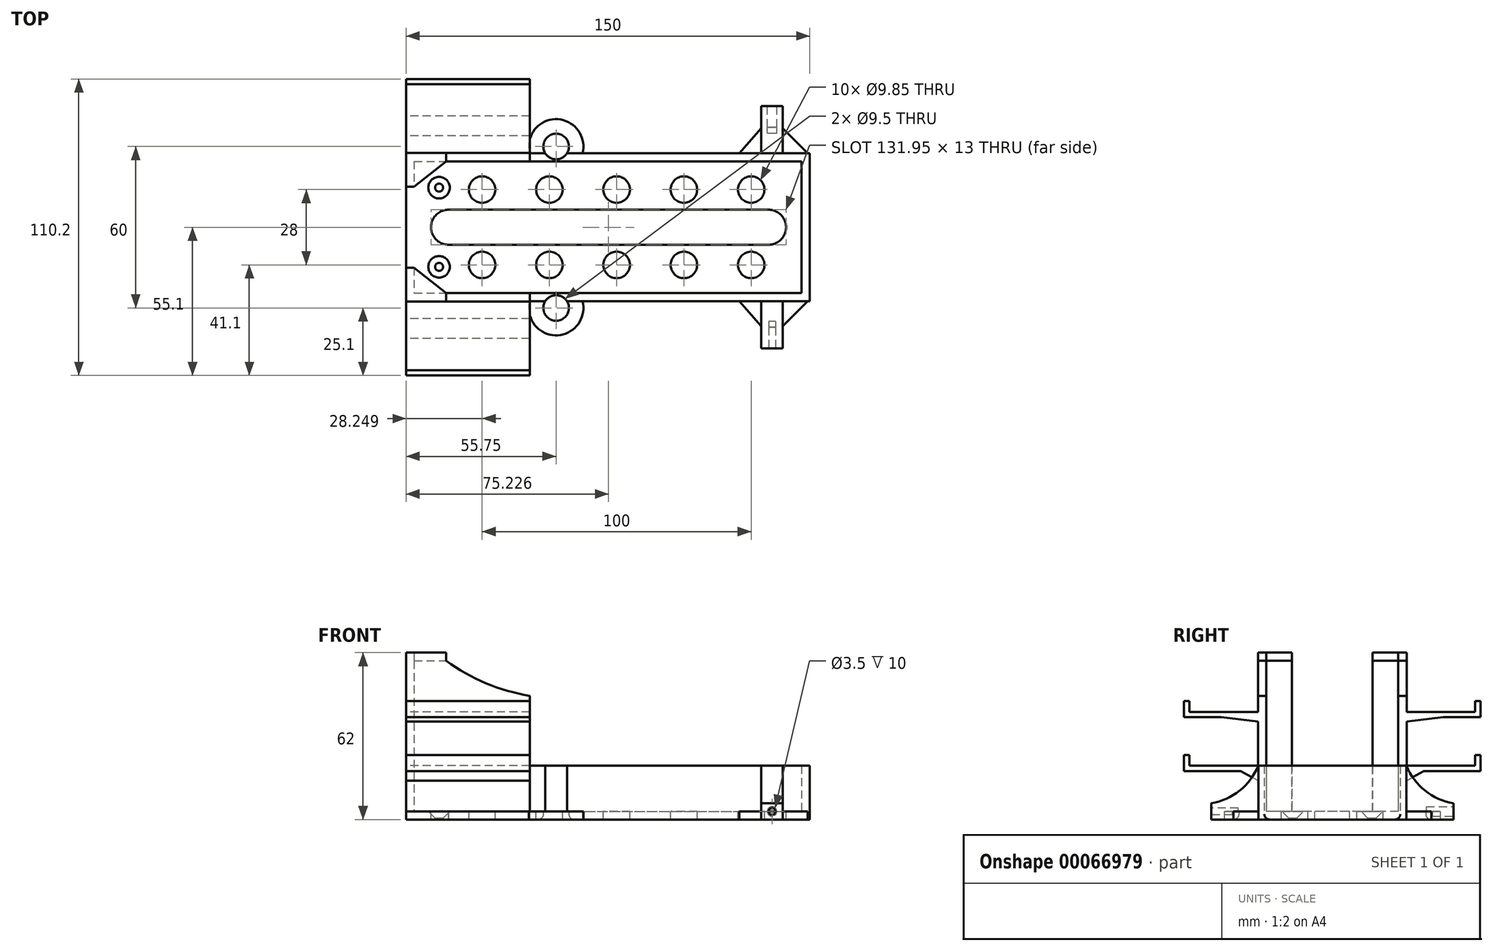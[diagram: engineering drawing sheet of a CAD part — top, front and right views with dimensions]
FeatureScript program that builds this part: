
annotation { "Feature Type Name" : "Feature", "Feature Type Description" : "" }
export const myFeature = defineFeature(function(context is Context, id is Id, definition is map)
    precondition{}
    {
        {
            var Q0;
            Q0=qCreatedBy(makeId("Top.planeOp"),FACE);
            var sketch = newSketch(context, id + "F0", { "sketchPlane" : qUnion([Q0])});
            skLineSegment(sketch, "E0.bottom", {"start": v(0, 27.5) * mm, "end": v(150, 27.5) * mm});
            skLineSegment(sketch, "E0.top", {"start": v(0, -27.5) * mm, "end": v(150, -27.5) * mm});
            skLineSegment(sketch, "E0.left", {"start": v(0, 27.5) * mm, "end": v(0, -27.5) * mm});
            skLineSegment(sketch, "E0.right", {"start": v(150, 27.5) * mm, "end": v(150, -27.5) * mm});
            skLineSegment(sketch, "E1.0", {"start": v(3, 24.5) * mm, "end": v(147, 24.5) * mm});
            skLineSegment(sketch, "E1.1", {"start": v(3, 24.5) * mm, "end": v(3, -24.5) * mm});
            skLineSegment(sketch, "E1.2", {"start": v(3, -24.5) * mm, "end": v(147, -24.5) * mm});
            skLineSegment(sketch, "E1.3", {"start": v(147, 24.5) * mm, "end": v(147, -24.5) * mm});
            skSolve(sketch);
        }
        {
            var Q0;
            Q0 = qSketchRegion(id + "F0", true);
            extrude(context, id + "F1", {"entities" : qUnion([Q0]), "depth" : 20 * mm});
        }
        {
            var Q0;
            Q0=qCreatedBy(makeId("Top.planeOp"),FACE);
            var sketch = newSketch(context, id + "F2", { "sketchPlane" : qUnion([Q0])});
            skLineSegment(sketch, "E2.bottom", {"start": v(0, 27.5) * mm, "end": v(45.9, 27.5) * mm});
            skLineSegment(sketch, "E2.left", {"start": v(0, 27.5) * mm, "end": v(0, -27.5) * mm});
            skLineSegment(sketch, "E2.right", {"start": v(150, 27.5) * mm, "end": v(150, -27.5) * mm});
            skCircle(sketch, "E3", {"center": v(55.75, 30) * mm, "radius": 4.75 * mm});
            skArc(sketch, "E4", {"start": v(65.6, 27.5) * mm, "mid": v(55.75, 40.16) * mm, "end": v(45.9, 27.5) * mm});
            skLineSegment(sketch, "E5.trimOffspring", {"start": v(65.6, 27.5) * mm, "end": v(150, 27.5) * mm});
            skLineSegment(sketch, "E6.MirrorCS", {"start": v(0, -27.5) * mm, "end": v(45.9, -27.5) * mm});
            skLineSegment(sketch, "E7.MirrorCS", {"start": v(65.6, -27.5) * mm, "end": v(150, -27.5) * mm});
            skCircle(sketch, "E8.MirrorC", {"center": v(55.75, -30) * mm, "radius": 4.75 * mm});
            skArc(sketch, "E9.MirrorCS", {"start": v(65.6, -27.5) * mm, "mid": v(55.75, -40.16) * mm, "end": v(45.9, -27.5) * mm});
            skSolve(sketch);
        }
        {
            var Q0;
            Q0=qCreatedBy(makeId("Top.planeOp"),FACE);
            var sketch = newSketch(context, id + "F3", { "sketchPlane" : qUnion([Q0])});
            skCircle(sketch, "E10", {"center": v(55.75, 30) * mm, "radius": 4.75 * mm});
            skCircle(sketch, "E11.MirrorC", {"center": v(55.75, -30) * mm, "radius": 4.75 * mm});
            skSolve(sketch);
        }
        {
            var Q0;
            Q0 = qSketchRegion(id + "F3", true);
            extrude(context, id + "F4", {"entities" : qUnion([Q0]), "operationType" : NewBodyOperationType.REMOVE, "depth" : 25 * mm});
        }
        {
            var Q0;
            Q0=qCreatedBy(makeId("Top.planeOp"),FACE);
            var sketch = newSketch(context, id + "F5", { "sketchPlane" : qUnion([Q0])});
            skLineSegment(sketch, "E12.bottom", {"start": v(140, 45) * mm, "end": v(132, 45) * mm});
            skLineSegment(sketch, "E12.top", {"start": v(140, -45) * mm, "end": v(132, -45) * mm});
            skLineSegment(sketch, "E12.left", {"start": v(140, 45) * mm, "end": v(140, 25.62) * mm});
            skLineSegment(sketch, "E12.right", {"start": v(132, 45) * mm, "end": v(132, 25.62) * mm});
            skLineSegment(sketch, "E13", {"start": v(132, 25.62) * mm, "end": v(140, 25.62) * mm});
            skLineSegment(sketch, "E14.MirrorCS", {"start": v(132, -25.62) * mm, "end": v(140, -25.62) * mm});
            skLineSegment(sketch, "E15.trimOffspring", {"start": v(132, -25.62) * mm, "end": v(132, -45) * mm});
            skLineSegment(sketch, "E16.trimOffspring", {"start": v(140, -25.62) * mm, "end": v(140, -45) * mm});
            skSolve(sketch);
        }
        {
            var Q0;
            Q0 = qSketchRegion(id + "F5", true);
            extrude(context, id + "F6", {"entities" : qUnion([Q0]), "operationType" : NewBodyOperationType.ADD, "depth" : 20 * mm});
        }
        {
            var Q0;
            Q0=makeQuery(id+"F6.opExtrude","SWEPT_FACE",FACE,{"disambiguationData":[OSD([sQuery(id+"F5.wireOp",EDGE,"E12.left")])]});
            var sketch = newSketch(context, id + "F7", { "sketchPlane" : qUnion([Q0])});
            skPoint(sketch, "E17.endSnap0", {"position": v(36.25, 0) * mm});
            skArc(sketch, "E18", {"start": v(27.5, 20) * mm, "mid": v(34.45, 10.75) * mm, "end": v(45, 6) * mm});
            skLineSegment(sketch, "E19", {"start": v(45, 6) * mm, "end": v(45, 20) * mm});
            skLineSegment(sketch, "E20", {"start": v(45, 20) * mm, "end": v(27.5, 20) * mm});
            skLineSegment(sketch, "E21.MirrorCS", {"start": v(-45, 20) * mm, "end": v(-27.5, 20) * mm});
            skPoint(sketch, "E22.MirrorP", {"position": v(-36.25, 0) * mm});
            skArc(sketch, "E23.MirrorCS", {"start": v(-27.5, 20) * mm, "mid": v(-34.45, 10.75) * mm, "end": v(-45, 6) * mm});
            skLineSegment(sketch, "E24.MirrorCS", {"start": v(-45, 6) * mm, "end": v(-45, 20) * mm});
            skSolve(sketch);
        }
        {
            var Q0;
            Q0 = qSketchRegion(id + "F7", true);
            extrude(context, id + "F8", {"entities" : qUnion([Q0]), "operationType" : NewBodyOperationType.REMOVE, "oppositeDirection" : true, "depth" : 25 * mm});
        }
        {
            var Q0;
            Q0 = qSketchRegion(id + "F2", true);
            extrude(context, id + "F9", {"entities" : qUnion([Q0]), "operationType" : NewBodyOperationType.ADD, "depth" : 3 * mm});
        }
        {
            var Q0;
            Q0=makeQuery(id+"F9.boolean.opBoolean","MERGE",EDGE,{"derivedFrom":[makeQuery(id+"F4.boolean.opBoolean","COPY",EDGE,{"derivedFrom":makeQuery(id+"F4.opExtrude","CAP_EDGE",EDGE,{"disambiguationData":[OSD([sQuery(id+"F3.wireOp",EDGE,"E10")])],"isStart":true})}),makeQuery(id+"F9.opExtrude","CAP_EDGE",EDGE,{"disambiguationData":[OSD([sQuery(id+"F2.wireOp",EDGE,"E3")])],"isStart":true})]});
            var Q1;
            Q1=makeQuery(id+"F9.boolean.opBoolean","MERGE",EDGE,{"derivedFrom":[makeQuery(id+"F4.boolean.opBoolean","COPY",EDGE,{"derivedFrom":makeQuery(id+"F4.opExtrude","CAP_EDGE",EDGE,{"disambiguationData":[OSD([sQuery(id+"F3.wireOp",EDGE,"E11.MirrorC")])],"isStart":true})}),makeQuery(id+"F9.opExtrude","CAP_EDGE",EDGE,{"disambiguationData":[OSD([sQuery(id+"F2.wireOp",EDGE,"E8.MirrorC")])],"isStart":true})]});
            fillet(context, id + "F10", {"entities" : qUnion([Q0, Q1]), "radius" : 2 * mm, "tangentPropagation" : true, "allowEdgeOverflow" : false});
        }
        {
            var Q0;
            Q0=makeQuery(id+"F9.boolean.opBoolean","SPLIT",FACE,{"disambiguationData":[TD([makeQuery(id+"F1.opExtrude","SWEPT_FACE",FACE,{"disambiguationData":[OSD([sQuery(id+"F0.wireOp",EDGE,"E1.0")])]})])],"derivedFrom":makeQuery(id+"F9.opExtrude","CAP_FACE",FACE,{"disambiguationData":[OSD([sQuery(id+"F2.wireOp",EDGE,"E2.bottom"),sQuery(id+"F2.wireOp",EDGE,"E2.left"),sQuery(id+"F2.wireOp",EDGE,"E2.right"),sQuery(id+"F2.wireOp",EDGE,"E3"),sQuery(id+"F2.wireOp",EDGE,"E4"),sQuery(id+"F2.wireOp",EDGE,"E5.trimOffspring"),sQuery(id+"F2.wireOp",EDGE,"E6.MirrorCS"),sQuery(id+"F2.wireOp",EDGE,"E7.MirrorCS"),sQuery(id+"F2.wireOp",EDGE,"E8.MirrorC"),sQuery(id+"F2.wireOp",EDGE,"E9.MirrorCS")])],"isStart":false})});
            var sketch = newSketch(context, id + "F11", { "sketchPlane" : qUnion([Q0])});
            skLineSegment(sketch, "E25", {"start": v(0, 27.6) * mm, "end": v(45.98, 27.6) * mm});
            skLineSegment(sketch, "E26", {"start": v(45.98, 27.6) * mm, "end": v(45.98, 24.5) * mm});
            skLineSegment(sketch, "E27", {"start": v(45.98, 24.5) * mm, "end": v(3, 24.5) * mm});
            skLineSegment(sketch, "E28", {"start": v(3, 24.5) * mm, "end": v(3, 0) * mm});
            skLineSegment(sketch, "E29", {"start": v(0, 0) * mm, "end": v(0, 27.6) * mm});
            skLineSegment(sketch, "E30.MirrorCS", {"start": v(0, -27.6) * mm, "end": v(45.98, -27.6) * mm});
            skLineSegment(sketch, "E31.MirrorCS", {"start": v(45.98, -24.5) * mm, "end": v(3, -24.5) * mm});
            skLineSegment(sketch, "E32.MirrorCS", {"start": v(45.98, -27.6) * mm, "end": v(45.98, -24.5) * mm});
            skLineSegment(sketch, "E33.MirrorCS", {"start": v(3, -24.5) * mm, "end": v(3, 0) * mm});
            skLineSegment(sketch, "E34.MirrorCS", {"start": v(0, 0) * mm, "end": v(0, -27.6) * mm});
            skSolve(sketch);
        }
        {
            var Q0;
            Q0 = qSketchRegion(id + "F11", true);
            extrude(context, id + "F12", {"entities" : qUnion([Q0]), "operationType" : NewBodyOperationType.ADD, "depth" : 56 * mm});
        }
        {
            var Q0;
            Q0=makeQuery(id+"F12.boolean.opBoolean","MERGE",FACE,{"derivedFrom":[makeQuery(id+"F1.opExtrude","SWEPT_FACE",FACE,{"disambiguationData":[OSD([sQuery(id+"F0.wireOp",EDGE,"E0.left")])]}),makeQuery(id+"F12.opExtrude","SWEPT_FACE",FACE,{"disambiguationData":[OSD([sQuery(id+"F11.wireOp",EDGE,"E29"),sQuery(id+"F11.wireOp",EDGE,"E34.MirrorCS")])]})]});
            var sketch = newSketch(context, id + "F13", { "sketchPlane" : qUnion([Q0])});
            skLineSegment(sketch, "E35", {"start": v(-15, 3) * mm, "end": v(15, 3) * mm});
            skLineSegment(sketch, "E36", {"start": v(-15, 3) * mm, "end": v(-15, 59) * mm});
            skLineSegment(sketch, "E37", {"start": v(-15, 59) * mm, "end": v(15, 59) * mm});
            skLineSegment(sketch, "E38", {"start": v(15, 59) * mm, "end": v(15, 3) * mm});
            skSolve(sketch);
        }
        {
            var Q0;
            Q0 = qSketchRegion(id + "F13", true);
            extrude(context, id + "F14", {"entities" : qUnion([Q0]), "operationType" : NewBodyOperationType.REMOVE, "oppositeDirection" : true, "depth" : 25 * mm});
        }
        {
            var Q0;
            {var subQ0=sQuery(id+"F11.wireOp",EDGE,"E25");var subQ1=sQuery(id+"F11.wireOp",EDGE,"E26");var subQ2=sQuery(id+"F11.wireOp",EDGE,"E34.MirrorCS");var subQ3=sQuery(id+"F11.wireOp",EDGE,"E29");var subQ4=sQuery(id+"F11.wireOp",EDGE,"E27");var subQ5=sQuery(id+"F11.wireOp",EDGE,"E33.MirrorCS");var subQ6=sQuery(id+"F11.wireOp",EDGE,"E28");Q0=makeQuery(id+"F14.boolean.opBoolean","SPLIT",FACE,{"disambiguationData":[TD([makeQuery(id+"F1.opExtrude","SWEPT_FACE",FACE,{"disambiguationData":[OSD([sQuery(id+"F0.wireOp",EDGE,"E1.0")])]})])],"derivedFrom":makeQuery(id+"F12.opExtrude","CAP_FACE",FACE,{"disambiguationData":[OSD([subQ0,subQ1,subQ4,subQ6,subQ3,sQuery(id+"F11.wireOp",EDGE,"E30.MirrorCS"),sQuery(id+"F11.wireOp",EDGE,"E31.MirrorCS"),sQuery(id+"F11.wireOp",EDGE,"E32.MirrorCS"),subQ5,subQ2])],"isStart":false})});}
            var sketch = newSketch(context, id + "F15", { "sketchPlane" : qUnion([Q0])});
            skLineSegment(sketch, "E39", {"start": v(3, 15) * mm, "end": v(14.86, 24.5) * mm});
            skLineSegment(sketch, "E40", {"start": v(14.86, 24.5) * mm, "end": v(14.86, 27.6) * mm});
            skLineSegment(sketch, "E41", {"start": v(14.86, 27.6) * mm, "end": v(0, 27.6) * mm});
            skLineSegment(sketch, "E42", {"start": v(0, 27.6) * mm, "end": v(0, 15) * mm});
            skLineSegment(sketch, "E43", {"start": v(0, 15) * mm, "end": v(3, 15) * mm});
            skLineSegment(sketch, "E44.MirrorCS", {"start": v(0, -15) * mm, "end": v(3, -15) * mm});
            skLineSegment(sketch, "E45.MirrorCS", {"start": v(14.86, -24.5) * mm, "end": v(14.86, -27.6) * mm});
            skLineSegment(sketch, "E46.MirrorCS", {"start": v(0, -27.6) * mm, "end": v(0, -15) * mm});
            skLineSegment(sketch, "E47.MirrorCS", {"start": v(3, -15) * mm, "end": v(14.86, -24.5) * mm});
            skLineSegment(sketch, "E48.MirrorCS", {"start": v(14.86, -27.6) * mm, "end": v(0, -27.6) * mm});
            skSolve(sketch);
        }
        {
            var Q0;
            Q0 = qSketchRegion(id + "F15", true);
            extrude(context, id + "F16", {"entities" : qUnion([Q0]), "operationType" : NewBodyOperationType.ADD, "depth" : 3 * mm});
        }
        {
            var Q0;
            Q0=makeQuery(id+"F14.boolean.opBoolean","MERGE",FACE,{"derivedFrom":[makeQuery(id+"F9.boolean.opBoolean","SPLIT",FACE,{"disambiguationData":[TD([makeQuery(id+"F1.opExtrude","SWEPT_FACE",FACE,{"disambiguationData":[OSD([sQuery(id+"F0.wireOp",EDGE,"E1.0")])]})])],"derivedFrom":makeQuery(id+"F9.opExtrude","CAP_FACE",FACE,{"disambiguationData":[OSD([sQuery(id+"F2.wireOp",EDGE,"E2.bottom"),sQuery(id+"F2.wireOp",EDGE,"E2.left"),sQuery(id+"F2.wireOp",EDGE,"E2.right"),sQuery(id+"F2.wireOp",EDGE,"E3"),sQuery(id+"F2.wireOp",EDGE,"E4"),sQuery(id+"F2.wireOp",EDGE,"E5.trimOffspring"),sQuery(id+"F2.wireOp",EDGE,"E6.MirrorCS"),sQuery(id+"F2.wireOp",EDGE,"E7.MirrorCS"),sQuery(id+"F2.wireOp",EDGE,"E8.MirrorC"),sQuery(id+"F2.wireOp",EDGE,"E9.MirrorCS")])],"isStart":false})}),makeQuery(id+"F14.opExtrude","SWEPT_FACE",FACE,{"disambiguationData":[OSD([sQuery(id+"F13.wireOp",EDGE,"E35")])]})]});
            var sketch = newSketch(context, id + "F17", { "sketchPlane" : qUnion([Q0])});
            skCircle(sketch, "E49", {"center": v(15.75, 0) * mm, "radius": 6 * mm});
            skCircle(sketch, "E50.1.0.0", {"center": v(40.75, 0) * mm, "radius": 6 * mm});
            skCircle(sketch, "E50.2.0.0", {"center": v(65.75, 0) * mm, "radius": 6 * mm});
            skCircle(sketch, "E50.3.0.0", {"center": v(90.75, 0) * mm, "radius": 6 * mm});
            skCircle(sketch, "E50.4.0.0", {"center": v(115.75, 0) * mm, "radius": 6 * mm});
            skLineSegment(sketch, "E50.direction1", {"start": v(15.75, 0) * mm, "end": v(40.75, 0) * mm, "construction": true});
            skCircle(sketch, "E51", {"center": v(28.25, 14) * mm, "radius": 4.93 * mm});
            skCircle(sketch, "E52.1.0.0", {"center": v(53.25, 14) * mm, "radius": 4.93 * mm});
            skCircle(sketch, "E52.2.0.0", {"center": v(78.25, 14) * mm, "radius": 4.93 * mm});
            skCircle(sketch, "E52.3.0.0", {"center": v(103.25, 14) * mm, "radius": 4.93 * mm});
            skCircle(sketch, "E52.4.0.0", {"center": v(128.25, 14) * mm, "radius": 4.93 * mm});
            skLineSegment(sketch, "E52.direction1", {"start": v(28.25, 14) * mm, "end": v(53.25, 14) * mm, "construction": true});
            skCircle(sketch, "E53.MirrorC", {"center": v(28.25, -14) * mm, "radius": 4.93 * mm});
            skCircle(sketch, "E54.MirrorC", {"center": v(53.25, -14) * mm, "radius": 4.93 * mm});
            skCircle(sketch, "E55.MirrorC", {"center": v(78.25, -14) * mm, "radius": 4.93 * mm});
            skCircle(sketch, "E56.MirrorC", {"center": v(103.25, -14) * mm, "radius": 4.93 * mm});
            skCircle(sketch, "E57.MirrorC", {"center": v(128.25, -14) * mm, "radius": 4.93 * mm});
            skSolve(sketch);
        }
        {
            var Q0;
            Q0 = qSketchRegion(id + "F17", true);
            extrude(context, id + "F18", {"entities" : qUnion([Q0]), "operationType" : NewBodyOperationType.REMOVE, "oppositeDirection" : true, "depth" : 25 * mm});
        }
        {
            var Q0;
            Q0=makeQuery(id+"F6.opExtrude","SWEPT_FACE",FACE,{"disambiguationData":[OSD([sQuery(id+"F5.wireOp",EDGE,"E12.top")])]});
            var sketch = newSketch(context, id + "F19", { "sketchPlane" : qUnion([Q0])});
            skCircle(sketch, "E58", {"center": v(136, 3) * mm, "radius": 1.25 * mm});
            skPoint(sketch, "E58.centerSnap0", {"position": v(132, 3) * mm});
            skPoint(sketch, "E58.centerSnap1", {"position": v(136, 6) * mm});
            skSolve(sketch);
        }
        {
            var Q0;
            Q0 = qSketchRegion(id + "F19", true);
            extrude(context, id + "F20", {"entities" : qUnion([Q0]), "operationType" : NewBodyOperationType.REMOVE, "oppositeDirection" : true, "depth" : 10 * mm});
        }
        {
            var Q0;
            Q0=makeQuery(id+"F6.opExtrude","SWEPT_FACE",FACE,{"disambiguationData":[OSD([sQuery(id+"F5.wireOp",EDGE,"E12.bottom")])]});
            var sketch = newSketch(context, id + "F21", { "sketchPlane" : qUnion([Q0])});
            skCircle(sketch, "E59", {"center": v(-136, 3) * mm, "radius": 1.75 * mm});
            skPoint(sketch, "E59.centerSnap0", {"position": v(-140, 3) * mm});
            skPoint(sketch, "E59.centerSnap1", {"position": v(-136, 6) * mm});
            skSolve(sketch);
        }
        {
            var Q0;
            Q0 = qSketchRegion(id + "F21", true);
            extrude(context, id + "F22", {"entities" : qUnion([Q0]), "operationType" : NewBodyOperationType.REMOVE, "oppositeDirection" : true, "depth" : 10 * mm});
        }
        {
            var Q0;
            Q0=makeQuery(id+"F14.boolean.opBoolean","MERGE",FACE,{"derivedFrom":[makeQuery(id+"F9.boolean.opBoolean","SPLIT",FACE,{"disambiguationData":[TD([makeQuery(id+"F1.opExtrude","SWEPT_FACE",FACE,{"disambiguationData":[OSD([sQuery(id+"F0.wireOp",EDGE,"E1.0")])]})])],"derivedFrom":makeQuery(id+"F9.opExtrude","CAP_FACE",FACE,{"disambiguationData":[OSD([sQuery(id+"F2.wireOp",EDGE,"E2.bottom"),sQuery(id+"F2.wireOp",EDGE,"E2.left"),sQuery(id+"F2.wireOp",EDGE,"E2.right"),sQuery(id+"F2.wireOp",EDGE,"E3"),sQuery(id+"F2.wireOp",EDGE,"E4"),sQuery(id+"F2.wireOp",EDGE,"E5.trimOffspring"),sQuery(id+"F2.wireOp",EDGE,"E6.MirrorCS"),sQuery(id+"F2.wireOp",EDGE,"E7.MirrorCS"),sQuery(id+"F2.wireOp",EDGE,"E8.MirrorC"),sQuery(id+"F2.wireOp",EDGE,"E9.MirrorCS")])],"isStart":false})}),makeQuery(id+"F14.opExtrude","SWEPT_FACE",FACE,{"disambiguationData":[OSD([sQuery(id+"F13.wireOp",EDGE,"E35")])]})]});
            var sketch = newSketch(context, id + "F23", { "sketchPlane" : qUnion([Q0])});
            skPoint(sketch, "E60", {"position": v(12.26, 14.71) * mm});
            skPoint(sketch, "E61.MirrorP", {"position": v(12.26, -14.71) * mm});
            skSolve(sketch);
        }
        {
            var Q0;
            Q0=sQuery(id+"F23.wireOp",VERTEX,"E60");
            var Q1;
            Q1=sQuery(id+"F23.wireOp",VERTEX,"E61.MirrorP");
            var Q2;
            Q2=makeQuery(id+"F1.opExtrude","SWEPT_BODY",BODY,{"disambiguationData":[OSD([sQuery(id+"F0.wireOp",EDGE,"E0.bottom"),sQuery(id+"F0.wireOp",EDGE,"E0.top"),sQuery(id+"F0.wireOp",EDGE,"E0.left"),sQuery(id+"F0.wireOp",EDGE,"E0.right"),sQuery(id+"F0.wireOp",EDGE,"E1.0"),sQuery(id+"F0.wireOp",EDGE,"E1.1"),sQuery(id+"F0.wireOp",EDGE,"E1.2"),sQuery(id+"F0.wireOp",EDGE,"E1.3")])]});
            hole(context, id + "F24", {"style" : HoleStyle.C_SINK, "holeDiameter" : 3 * mm, "cSinkDiameter" : 8 * mm, "endStyle" : HoleEndStyle.THROUGH, "locations" : qUnion([Q0, Q1]), "scope" : qUnion([Q2]), "cSinkAngle" : 90 * degree});
        }
        {
            var Q0;
            Q0=makeQuery(id+"F16.boolean.opBoolean","MERGE",FACE,{"derivedFrom":[makeQuery(id+"F12.boolean.opBoolean","MERGE",FACE,{"derivedFrom":[makeQuery(id+"F1.opExtrude","SWEPT_FACE",FACE,{"disambiguationData":[OSD([sQuery(id+"F0.wireOp",EDGE,"E0.left")])]}),makeQuery(id+"F12.opExtrude","SWEPT_FACE",FACE,{"disambiguationData":[OSD([sQuery(id+"F11.wireOp",EDGE,"E29"),sQuery(id+"F11.wireOp",EDGE,"E34.MirrorCS")])]})]}),makeQuery(id+"F16.opExtrude","SWEPT_FACE",FACE,{"disambiguationData":[OSD([sQuery(id+"F15.wireOp",EDGE,"E42")])]}),makeQuery(id+"F16.opExtrude","SWEPT_FACE",FACE,{"disambiguationData":[OSD([sQuery(id+"F15.wireOp",EDGE,"E46.MirrorCS")])]})]});
            var sketch = newSketch(context, id + "F25", { "sketchPlane" : qUnion([Q0])});
            skLineSegment(sketch, "E62", {"start": v(-55.1, 38) * mm, "end": v(-55.1, 44) * mm});
            skLineSegment(sketch, "E63", {"start": v(-55.1, 44) * mm, "end": v(-53.1, 44) * mm});
            skLineSegment(sketch, "E64", {"start": v(-53.1, 44) * mm, "end": v(-53.1, 40) * mm});
            skLineSegment(sketch, "E65", {"start": v(-53.1, 40) * mm, "end": v(-27.6, 40) * mm});
            skLineSegment(sketch, "E66", {"start": v(-55.1, 38) * mm, "end": v(-41.28, 38) * mm});
            skLineSegment(sketch, "E67", {"start": v(-27.6, 36.45) * mm, "end": v(-41.28, 38) * mm});
            skPoint(sketch, "E68", {"position": v(-27.6, 32.5) * mm});
            skLineSegment(sketch, "E69", {"start": v(-55.1, 18) * mm, "end": v(-34.02, 18) * mm});
            skLineSegment(sketch, "E70", {"start": v(-53.1, 20) * mm, "end": v(-27.6, 20) * mm});
            skLineSegment(sketch, "E71", {"start": v(-53.1, 24) * mm, "end": v(-53.1, 20) * mm});
            skLineSegment(sketch, "E72", {"start": v(-27.6, 14.45) * mm, "end": v(-34.02, 18) * mm});
            skLineSegment(sketch, "E73", {"start": v(-55.1, 18) * mm, "end": v(-55.1, 24) * mm});
            skPoint(sketch, "E74", {"position": v(-27.6, 16.5) * mm});
            skLineSegment(sketch, "E75", {"start": v(-55.1, 24) * mm, "end": v(-53.1, 24) * mm});
            skLineSegment(sketch, "E76.MirrorCS", {"start": v(53.1, 24) * mm, "end": v(53.1, 20) * mm});
            skLineSegment(sketch, "E77.MirrorCS", {"start": v(55.1, 24) * mm, "end": v(53.1, 24) * mm});
            skLineSegment(sketch, "E78.MirrorCS", {"start": v(55.1, 38) * mm, "end": v(55.1, 44) * mm});
            skLineSegment(sketch, "E79.MirrorCS", {"start": v(53.1, 44) * mm, "end": v(53.1, 40) * mm});
            skLineSegment(sketch, "E80.MirrorCS", {"start": v(55.1, 44) * mm, "end": v(53.1, 44) * mm});
            skLineSegment(sketch, "E81.MirrorCS", {"start": v(55.1, 18) * mm, "end": v(55.1, 24) * mm});
            skLineSegment(sketch, "E82.MirrorCS", {"start": v(55.1, 18) * mm, "end": v(34.02, 18) * mm});
            skLineSegment(sketch, "E83.MirrorCS", {"start": v(27.6, 14.45) * mm, "end": v(34.02, 18) * mm});
            skLineSegment(sketch, "E84.MirrorCS", {"start": v(27.6, 36.45) * mm, "end": v(41.28, 38) * mm});
            skLineSegment(sketch, "E85.MirrorCS", {"start": v(53.1, 40) * mm, "end": v(27.6, 40) * mm});
            skPoint(sketch, "E86.MirrorP", {"position": v(27.6, 16.5) * mm});
            skPoint(sketch, "E87.MirrorP", {"position": v(27.6, 32.5) * mm});
            skLineSegment(sketch, "E88.MirrorCS", {"start": v(55.1, 38) * mm, "end": v(41.28, 38) * mm});
            skLineSegment(sketch, "E89.MirrorCS", {"start": v(53.1, 20) * mm, "end": v(27.6, 20) * mm});
            skLineSegment(sketch, "E90", {"start": v(-27.6, 40) * mm, "end": v(-27.6, 36.45) * mm});
            skLineSegment(sketch, "E91", {"start": v(-27.6, 20) * mm, "end": v(-27.6, 14.45) * mm});
            skLineSegment(sketch, "E92", {"start": v(27.6, 40) * mm, "end": v(27.6, 36.45) * mm});
            skLineSegment(sketch, "E93", {"start": v(27.6, 20) * mm, "end": v(27.6, 14.45) * mm});
            skSolve(sketch);
        }
        {
            var Q0;
            Q0 = qSketchRegion(id + "F25", true);
            var Q1;
            Q1=makeQuery(id+"F12.opExtrude","SWEPT_FACE",FACE,{"disambiguationData":[OSD([sQuery(id+"F11.wireOp",EDGE,"E26")])]});
            extrude(context, id + "F26", {"entities" : qUnion([Q0]), "operationType" : NewBodyOperationType.ADD, "endBound" : BoundingType.UP_TO_SURFACE, "oppositeDirection" : true, "endBoundEntityFace" : qUnion([Q1]), "depth" : 25 * mm});
        }
        {
            var Q0;
            {var subQ8=sQuery(id+"F15.wireOp",EDGE,"E45.MirrorCS");var subQ12=sQuery(id+"F15.wireOp",EDGE,"E48.MirrorCS");var subQ14=sQuery(id+"F11.wireOp",EDGE,"E30.MirrorCS");Q0=makeQuery(id+"F26.boolean.opBoolean","SPLIT",FACE,{"disambiguationData":[TD([makeQuery(id+"F16.opExtrude","SWEPT_FACE",FACE,{"disambiguationData":[OSD([subQ8])]})])],"derivedFrom":makeQuery(id+"F16.boolean.opBoolean","MERGE",FACE,{"derivedFrom":[makeQuery(id+"F12.opExtrude","SWEPT_FACE",FACE,{"disambiguationData":[OSD([subQ14])]}),makeQuery(id+"F16.opExtrude","SWEPT_FACE",FACE,{"disambiguationData":[OSD([subQ12])]})]})});}
            var sketch = newSketch(context, id + "F27", { "sketchPlane" : qUnion([Q0])});
            skArc(sketch, "E94", {"start": v(14.86, 59) * mm, "mid": v(29.65, 50.64) * mm, "end": v(45.98, 45.97) * mm});
            skLineSegment(sketch, "E95", {"start": v(14.86, 59) * mm, "end": v(45.98, 59) * mm});
            skLineSegment(sketch, "E96", {"start": v(45.98, 59) * mm, "end": v(45.98, 45.97) * mm});
            skSolve(sketch);
        }
        {
            var Q0;
            Q0 = qSketchRegion(id + "F27", true);
            extrude(context, id + "F28", {"entities" : qUnion([Q0]), "operationType" : NewBodyOperationType.REMOVE, "endBound" : BoundingType.THROUGH_ALL, "oppositeDirection" : true, "depth" : 25 * mm});
        }
        {
            var Q0;
            Q0=makeQuery(id+"F14.boolean.opBoolean","MERGE",FACE,{"derivedFrom":[makeQuery(id+"F9.boolean.opBoolean","SPLIT",FACE,{"disambiguationData":[TD([makeQuery(id+"F1.opExtrude","SWEPT_FACE",FACE,{"disambiguationData":[OSD([sQuery(id+"F0.wireOp",EDGE,"E1.0")])]})])],"derivedFrom":makeQuery(id+"F9.opExtrude","CAP_FACE",FACE,{"disambiguationData":[OSD([sQuery(id+"F2.wireOp",EDGE,"E2.bottom"),sQuery(id+"F2.wireOp",EDGE,"E2.left"),sQuery(id+"F2.wireOp",EDGE,"E2.right"),sQuery(id+"F2.wireOp",EDGE,"E3"),sQuery(id+"F2.wireOp",EDGE,"E4"),sQuery(id+"F2.wireOp",EDGE,"E5.trimOffspring"),sQuery(id+"F2.wireOp",EDGE,"E6.MirrorCS"),sQuery(id+"F2.wireOp",EDGE,"E7.MirrorCS"),sQuery(id+"F2.wireOp",EDGE,"E8.MirrorC"),sQuery(id+"F2.wireOp",EDGE,"E9.MirrorCS")])],"isStart":false})}),makeQuery(id+"F14.opExtrude","SWEPT_FACE",FACE,{"disambiguationData":[OSD([sQuery(id+"F13.wireOp",EDGE,"E35")])]})]});
            var sketch = newSketch(context, id + "F29", { "sketchPlane" : qUnion([Q0])});
            skArc(sketch, "E97", {"start": v(15.82, 6.5) * mm, "mid": v(9.25, -0.02) * mm, "end": v(15.86, -6.5) * mm});
            skArc(sketch, "E98", {"start": v(134.7, -6.5) * mm, "mid": v(141.2, 0) * mm, "end": v(134.7, 6.5) * mm});
            skLineSegment(sketch, "E99", {"start": v(15.68, 6.5) * mm, "end": v(134.7, 6.5) * mm});
            skLineSegment(sketch, "E100", {"start": v(15.86, -6.5) * mm, "end": v(134.7, -6.5) * mm});
            skSolve(sketch);
        }
        {
            var Q0;
            Q0 = qSketchRegion(id + "F29", true);
            extrude(context, id + "F30", {"entities" : qUnion([Q0]), "operationType" : NewBodyOperationType.REMOVE, "endBound" : BoundingType.THROUGH_ALL, "oppositeDirection" : true, "depth" : 25 * mm});
        }
        {
            var Q0;
            Q0=makeQuery(id+"F5.imprint","IMPRINT",FACE,{"disambiguationData":[TD([[makeQuery(id+"F5.imprint","IMPRINT",EDGE,{"derivedFrom":sQuery(id+"F5.wireOp",EDGE,"E12.top")}),-1.0]])]});
            var sketch = newSketch(context, id + "F31", { "sketchPlane" : qUnion([Q0])});
            skLineSegment(sketch, "E101", {"start": v(149.65, -27.14) * mm, "end": v(139.58, -37.2) * mm});
            skLineSegment(sketch, "E102", {"start": v(139.58, -37.2) * mm, "end": v(132.35, -37.2) * mm});
            skLineSegment(sketch, "E103", {"start": v(132.35, -37.2) * mm, "end": v(123.59, -27.2) * mm});
            skLineSegment(sketch, "E104", {"start": v(123.59, -27.2) * mm, "end": v(149.65, -27.14) * mm});
            skLineSegment(sketch, "E105.MirrorCS", {"start": v(139.58, 37.2) * mm, "end": v(132.35, 37.2) * mm});
            skLineSegment(sketch, "E106.MirrorCS", {"start": v(132.35, 37.2) * mm, "end": v(123.59, 27.2) * mm});
            skLineSegment(sketch, "E107.MirrorCS", {"start": v(149.65, 27.14) * mm, "end": v(139.58, 37.2) * mm});
            skLineSegment(sketch, "E108.MirrorCS", {"start": v(123.59, 27.2) * mm, "end": v(149.65, 27.14) * mm});
            skSolve(sketch);
        }
        {
            var Q0;
            Q0 = qSketchRegion(id + "F31", true);
            extrude(context, id + "F32", {"entities" : qUnion([Q0]), "operationType" : NewBodyOperationType.ADD, "depth" : 3 * mm});
        }
    });
